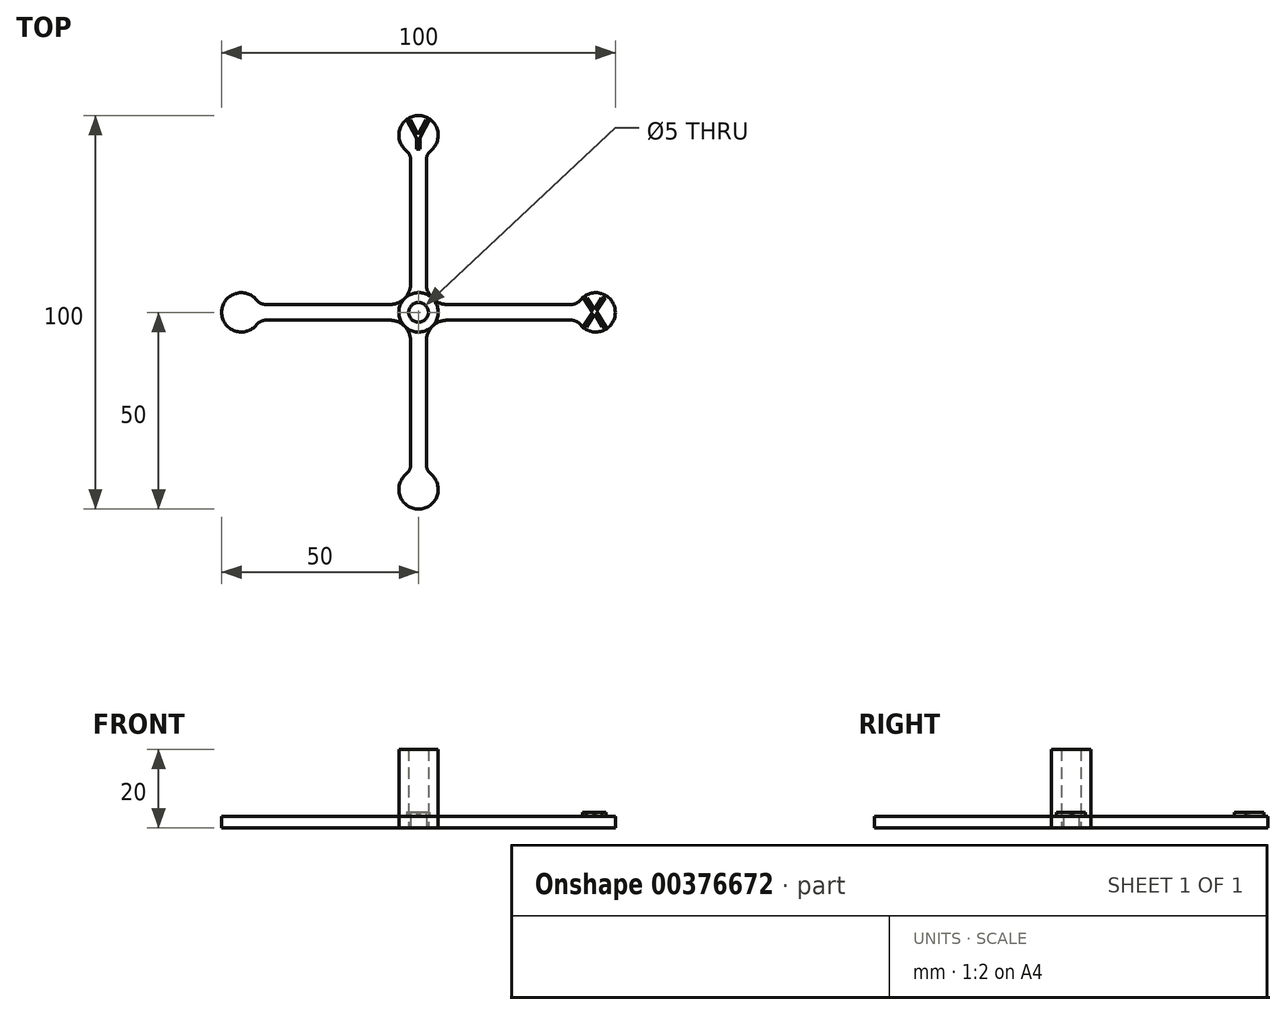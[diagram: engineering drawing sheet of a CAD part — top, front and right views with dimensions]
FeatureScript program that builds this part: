
annotation { "Feature Type Name" : "Feature", "Feature Type Description" : "" }
export const myFeature = defineFeature(function(context is Context, id is Id, definition is map)
    precondition{}
    {
        {
            var Q0;
            Q0=qCreatedBy(makeId("Top.planeOp"),FACE);
            var sketch = newSketch(context, id + "F0", { "sketchPlane" : qUnion([Q0])});
            skLineSegment(sketch, "E0.left", {"start": v(-2, 7.24) * mm, "end": v(-2, 38.76) * mm});
            skLineSegment(sketch, "E0.right", {"start": v(2, 7.24) * mm, "end": v(2, 38.76) * mm});
            skArc(sketch, "E1", {"start": v(3.12, 41.1) * mm, "mid": v(0, 50) * mm, "end": v(-3.13, 41.1) * mm});
            skArc(sketch, "E2.1.0", {"start": v(41.1, -3.12) * mm, "mid": v(50, 0) * mm, "end": v(41.1, 3.13) * mm});
            skLineSegment(sketch, "E2.1.1", {"start": v(7.24, -2) * mm, "end": v(38.76, -2) * mm});
            skLineSegment(sketch, "E2.1.2", {"start": v(7.24, 2) * mm, "end": v(38.76, 2) * mm});
            skArc(sketch, "E2.2.0", {"start": v(-3.12, -41.1) * mm, "mid": v(0, -50) * mm, "end": v(3.13, -41.1) * mm});
            skLineSegment(sketch, "E2.2.1", {"start": v(-2, -7.24) * mm, "end": v(-2, -38.76) * mm});
            skLineSegment(sketch, "E2.2.2", {"start": v(2, -7.24) * mm, "end": v(2, -38.76) * mm});
            skArc(sketch, "E2.3.0", {"start": v(-41.1, 3.12) * mm, "mid": v(-50, 0) * mm, "end": v(-41.1, -3.13) * mm});
            skLineSegment(sketch, "E2.3.1", {"start": v(-7.24, 2) * mm, "end": v(-38.76, 2) * mm});
            skLineSegment(sketch, "E2.3.2", {"start": v(-7.24, -2) * mm, "end": v(-38.76, -2) * mm});
            skPoint(sketch, "E2.center", {"position": v(0, 0) * mm});
            skPoint(sketch, "E3.orphan", {"position": v(2, 0) * mm});
            skPoint(sketch, "E0.bottom.start.orphan", {"position": v(-2, 0) * mm});
            skPoint(sketch, "E4.visualSharp", {"position": v(-40.42, 2) * mm});
            skArc(sketch, "E4.filletArc", {"start": v(-41.1, 3.12) * mm, "mid": v(-40.05, 2.3) * mm, "end": v(-38.76, 2) * mm});
            skCircle(sketch, "E5", {"center": v(0, 0) * mm, "radius": 50 * mm, "construction": true});
            skLineSegment(sketch, "E6", {"start": v(-45, 0) * mm, "end": v(45, 0) * mm, "construction": true});
            skLineSegment(sketch, "E7", {"start": v(0, -45) * mm, "end": v(0, 45) * mm, "construction": true});
            skPoint(sketch, "E8.visualSharp", {"position": v(-40.42, -2) * mm});
            skArc(sketch, "E8.filletArc", {"start": v(-38.76, -2) * mm, "mid": v(-40.05, -2.3) * mm, "end": v(-41.1, -3.12) * mm});
            skPoint(sketch, "E9.visualSharp", {"position": v(-2, -40.42) * mm});
            skArc(sketch, "E9.filletArc", {"start": v(-3.12, -41.1) * mm, "mid": v(-2.3, -40.05) * mm, "end": v(-2, -38.76) * mm});
            skPoint(sketch, "E10.visualSharp", {"position": v(2, -40.42) * mm});
            skArc(sketch, "E10.filletArc", {"start": v(2, -38.76) * mm, "mid": v(2.3, -40.05) * mm, "end": v(3.13, -41.1) * mm});
            skPoint(sketch, "E11.visualSharp", {"position": v(40.42, -2) * mm});
            skArc(sketch, "E11.filletArc", {"start": v(41.1, -3.13) * mm, "mid": v(40.05, -2.3) * mm, "end": v(38.76, -2) * mm});
            skPoint(sketch, "E12.visualSharp", {"position": v(40.42, 2) * mm});
            skArc(sketch, "E12.filletArc", {"start": v(38.76, 2) * mm, "mid": v(40.05, 2.3) * mm, "end": v(41.1, 3.12) * mm});
            skPoint(sketch, "E13.visualSharp", {"position": v(-2, 40.42) * mm});
            skArc(sketch, "E13.filletArc", {"start": v(-2, 38.76) * mm, "mid": v(-2.3, 40.05) * mm, "end": v(-3.13, 41.1) * mm});
            skPoint(sketch, "E14.visualSharp", {"position": v(2, 40.42) * mm});
            skArc(sketch, "E14.filletArc", {"start": v(3.12, 41.1) * mm, "mid": v(2.3, 40.05) * mm, "end": v(2, 38.76) * mm});
            skPoint(sketch, "E15.visualSharp", {"position": v(-2, 2) * mm});
            skArc(sketch, "E15.filletArc", {"start": v(-7.24, 2) * mm, "mid": v(-3.54, 3.54) * mm, "end": v(-2, 7.24) * mm});
            skPoint(sketch, "E16.visualSharp", {"position": v(2, 2) * mm});
            skArc(sketch, "E16.filletArc", {"start": v(2, 7.24) * mm, "mid": v(3.54, 3.54) * mm, "end": v(7.24, 2) * mm});
            skPoint(sketch, "E17.visualSharp", {"position": v(-2, -2) * mm});
            skArc(sketch, "E17.filletArc", {"start": v(-2, -7.24) * mm, "mid": v(-3.54, -3.54) * mm, "end": v(-7.24, -2) * mm});
            skPoint(sketch, "E18.visualSharp", {"position": v(2, -2) * mm});
            skArc(sketch, "E18.filletArc", {"start": v(7.24, -2) * mm, "mid": v(3.54, -3.54) * mm, "end": v(2, -7.24) * mm});
            skCircle(sketch, "E19", {"center": v(0, 0) * mm, "radius": 5 * mm});
            skCircle(sketch, "E20", {"center": v(0, 0) * mm, "radius": 2.5 * mm});
            skSolve(sketch);
        }
        {
            var Q0;
            Q0=makeQuery(id+"F0.imprint","IMPRINT",FACE,{"disambiguationData":[TD([[makeQuery(id+"F0.imprint","IMPRINT",EDGE,{"derivedFrom":sQuery(id+"F0.wireOp",EDGE,"E0.left")}),-1.0]])]});
            var Q1;
            Q1=makeQuery(id+"F0.imprint","IMPRINT",FACE,{"disambiguationData":[TD([[makeQuery(id+"F0.imprint","IMPRINT",EDGE,{"derivedFrom":sQuery(id+"F0.wireOp",EDGE,"E2.3.0")}),1.0]])]});
            var Q2;
            Q2=makeQuery(id+"F0.imprint","IMPRINT",FACE,{"disambiguationData":[TD([[makeQuery(id+"F0.imprint","IMPRINT",EDGE,{"derivedFrom":sQuery(id+"F0.wireOp",EDGE,"E2.1.0")}),1.0]])]});
            var Q3;
            Q3=makeQuery(id+"F0.imprint","IMPRINT",FACE,{"disambiguationData":[TD([[makeQuery(id+"F0.imprint","IMPRINT",EDGE,{"derivedFrom":sQuery(id+"F0.wireOp",EDGE,"E2.2.0")}),1.0]])]});
            var Q4;
            {var subQ0=sQuery(id+"F0.wireOp",EDGE,"E19");var subQ1=makeQuery(id+"F0.imprint","INTERSECT",VERTEX,{"derivedFrom":[sQuery(id+"F0.wireOp",EDGE,"E15.filletArc"),subQ0]});Q4=makeQuery(id+"F0.imprint","IMPRINT",FACE,{"disambiguationData":[TD([[makeQuery(id+"F0.imprint","IMPRINT",EDGE,{"disambiguationData":[TD([[subQ1,1.0]])],"derivedFrom":subQ0}),1.0]])]});}
            extrude(context, id + "F1", {"entities" : qUnion([Q0, Q1, Q2, Q3, Q4]), "depth" : 3 * mm, "offsetDistance" : 25 * mm});
        }
        {
            var Q0;
            Q0=makeQuery(id+"F1.opExtrude","CAP_FACE",FACE,{"disambiguationData":[OSD([sQuery(id+"F0.wireOp",EDGE,"E0.left"),sQuery(id+"F0.wireOp",EDGE,"E0.right"),sQuery(id+"F0.wireOp",EDGE,"E1"),sQuery(id+"F0.wireOp",EDGE,"E2.1.0"),sQuery(id+"F0.wireOp",EDGE,"E2.1.1"),sQuery(id+"F0.wireOp",EDGE,"E2.1.2"),sQuery(id+"F0.wireOp",EDGE,"E2.2.0"),sQuery(id+"F0.wireOp",EDGE,"E2.2.1"),sQuery(id+"F0.wireOp",EDGE,"E2.2.2"),sQuery(id+"F0.wireOp",EDGE,"E2.3.0"),sQuery(id+"F0.wireOp",EDGE,"E2.3.1"),sQuery(id+"F0.wireOp",EDGE,"E2.3.2"),sQuery(id+"F0.wireOp",EDGE,"E4.filletArc"),sQuery(id+"F0.wireOp",EDGE,"E8.filletArc"),sQuery(id+"F0.wireOp",EDGE,"E9.filletArc"),sQuery(id+"F0.wireOp",EDGE,"E10.filletArc"),sQuery(id+"F0.wireOp",EDGE,"E11.filletArc"),sQuery(id+"F0.wireOp",EDGE,"E12.filletArc"),sQuery(id+"F0.wireOp",EDGE,"E13.filletArc"),sQuery(id+"F0.wireOp",EDGE,"E14.filletArc"),sQuery(id+"F0.wireOp",EDGE,"EShmZOp4-N5FD-xiba-wA62-fkafupzrVAYz"),sQuery(id+"F0.wireOp",EDGE,"itGSDee8-mkRV-SKaI-ubbA-g03GVyBE4gpr"),sQuery(id+"F0.wireOp",EDGE,"tHYB3RTW-wbed-Nari-5iDj-zfRjz0G1ilCR"),sQuery(id+"F0.wireOp",EDGE,"KGa16Sfs-dR0K-ui6n-yG9d-uTp1EtkN7K44"),sQuery(id+"F0.wireOp",EDGE,"E15.filletArc"),sQuery(id+"F0.wireOp",EDGE,"E16.filletArc"),sQuery(id+"F0.wireOp",EDGE,"E17.filletArc"),sQuery(id+"F0.wireOp",EDGE,"E18.filletArc"),sQuery(id+"F0.wireOp",EDGE,"z9NT1NfI-LD79-IO8H-wwz2-yPxXgncybwza")])],"isStart":false});
            var sketch = newSketch(context, id + "F2", { "sketchPlane" : qUnion([Q0])});
            skText(sketch, "E21", { "text": "<-- Y AXIS", "fontName": "OpenSans-Regular.ttf"});
            skText(sketch, "E22", { "text": "X AXIS -->\n", "fontName": "OpenSans-Regular.ttf"});
            skText(sketch, "E23", { "text": "Y\n", "fontName": "OpenSans-Regular.ttf"});
            skText(sketch, "E24", { "text": "X", "fontName": "OpenSans-Regular.ttf"});
            const initialGuessF2  = {"E21": [-0.002, 0.0349, 0, -1, 0.004], "E22": [0.01056, -0.002, 1, 0, 0.004], "E23": [-0.003, 0.04148, 1, 0, 0.00753], "E24": [0.04168, -0.00375, 1, 0, 0.00748]};
            skSetInitialGuess(sketch, initialGuessF2);
            skSolve(sketch);
        }
        {
            var Q0;
            Q0=makeQuery(id+"F2.imprint","IMPRINT",FACE,{"disambiguationData":[TD([[makeQuery(id+"F2.imprint","IMPRINT",EDGE,{"derivedFrom":sQuery(id+"F2.wireOp",EDGE,"E23.sketch_text.stroke-0")}),-1.0]])]});
            var Q1;
            Q1=makeQuery(id+"F2.imprint","IMPRINT",FACE,{"disambiguationData":[TD([[makeQuery(id+"F2.imprint","IMPRINT",EDGE,{"derivedFrom":sQuery(id+"F2.wireOp",EDGE,"E24.sketch_text.stroke-0")}),-1.0]])]});
            extrude(context, id + "F3", {"entities" : qUnion([Q0, Q1]), "operationType" : NewBodyOperationType.ADD, "depth" : 1 * mm, "offsetDistance" : 25 * mm});
        }
        {
            var Q0;
            Q0=makeQuery(id+"F1.opExtrude","CAP_FACE",FACE,{"disambiguationData":[OSD([sQuery(id+"F0.wireOp",EDGE,"E0.left"),sQuery(id+"F0.wireOp",EDGE,"E0.right"),sQuery(id+"F0.wireOp",EDGE,"E1"),sQuery(id+"F0.wireOp",EDGE,"E2.1.0"),sQuery(id+"F0.wireOp",EDGE,"E2.1.1"),sQuery(id+"F0.wireOp",EDGE,"E2.1.2"),sQuery(id+"F0.wireOp",EDGE,"E2.2.0"),sQuery(id+"F0.wireOp",EDGE,"E2.2.1"),sQuery(id+"F0.wireOp",EDGE,"E2.2.2"),sQuery(id+"F0.wireOp",EDGE,"E2.3.0"),sQuery(id+"F0.wireOp",EDGE,"E2.3.1"),sQuery(id+"F0.wireOp",EDGE,"E2.3.2"),sQuery(id+"F0.wireOp",EDGE,"E4.filletArc"),sQuery(id+"F0.wireOp",EDGE,"E8.filletArc"),sQuery(id+"F0.wireOp",EDGE,"E9.filletArc"),sQuery(id+"F0.wireOp",EDGE,"E10.filletArc"),sQuery(id+"F0.wireOp",EDGE,"E11.filletArc"),sQuery(id+"F0.wireOp",EDGE,"E12.filletArc"),sQuery(id+"F0.wireOp",EDGE,"E13.filletArc"),sQuery(id+"F0.wireOp",EDGE,"E14.filletArc"),sQuery(id+"F0.wireOp",EDGE,"E15.filletArc"),sQuery(id+"F0.wireOp",EDGE,"E16.filletArc"),sQuery(id+"F0.wireOp",EDGE,"E17.filletArc"),sQuery(id+"F0.wireOp",EDGE,"E18.filletArc")])],"isStart":false});
            var sketch = newSketch(context, id + "F4", { "sketchPlane" : qUnion([Q0])});
            skCircle(sketch, "E25.0", {"center": v(0, 0) * mm, "radius": 5 * mm});
            skSolve(sketch);
        }
        {
            var Q0;
            {var subQ0=sQuery(id+"F4.wireOp",EDGE,"E25.0");var subQ1=makeQuery(id+"F4.imprint","INTERSECT",VERTEX,{"derivedFrom":[makeQuery(id+"F1.opExtrude","CAP_EDGE",EDGE,{"disambiguationData":[OSD([sQuery(id+"F0.wireOp",EDGE,"E15.filletArc")])],"isStart":false}),subQ0]});Q0=makeQuery(id+"F4.imprint","IMPRINT",FACE,{"disambiguationData":[TD([[makeQuery(id+"F4.imprint","IMPRINT",EDGE,{"disambiguationData":[TD([[subQ1,1.0]])],"derivedFrom":subQ0}),1.0]])]});}
            extrude(context, id + "F5", {"entities" : qUnion([Q0]), "operationType" : NewBodyOperationType.ADD, "depth" : 17 * mm, "offsetDistance" : 25 * mm});
        }
    });
